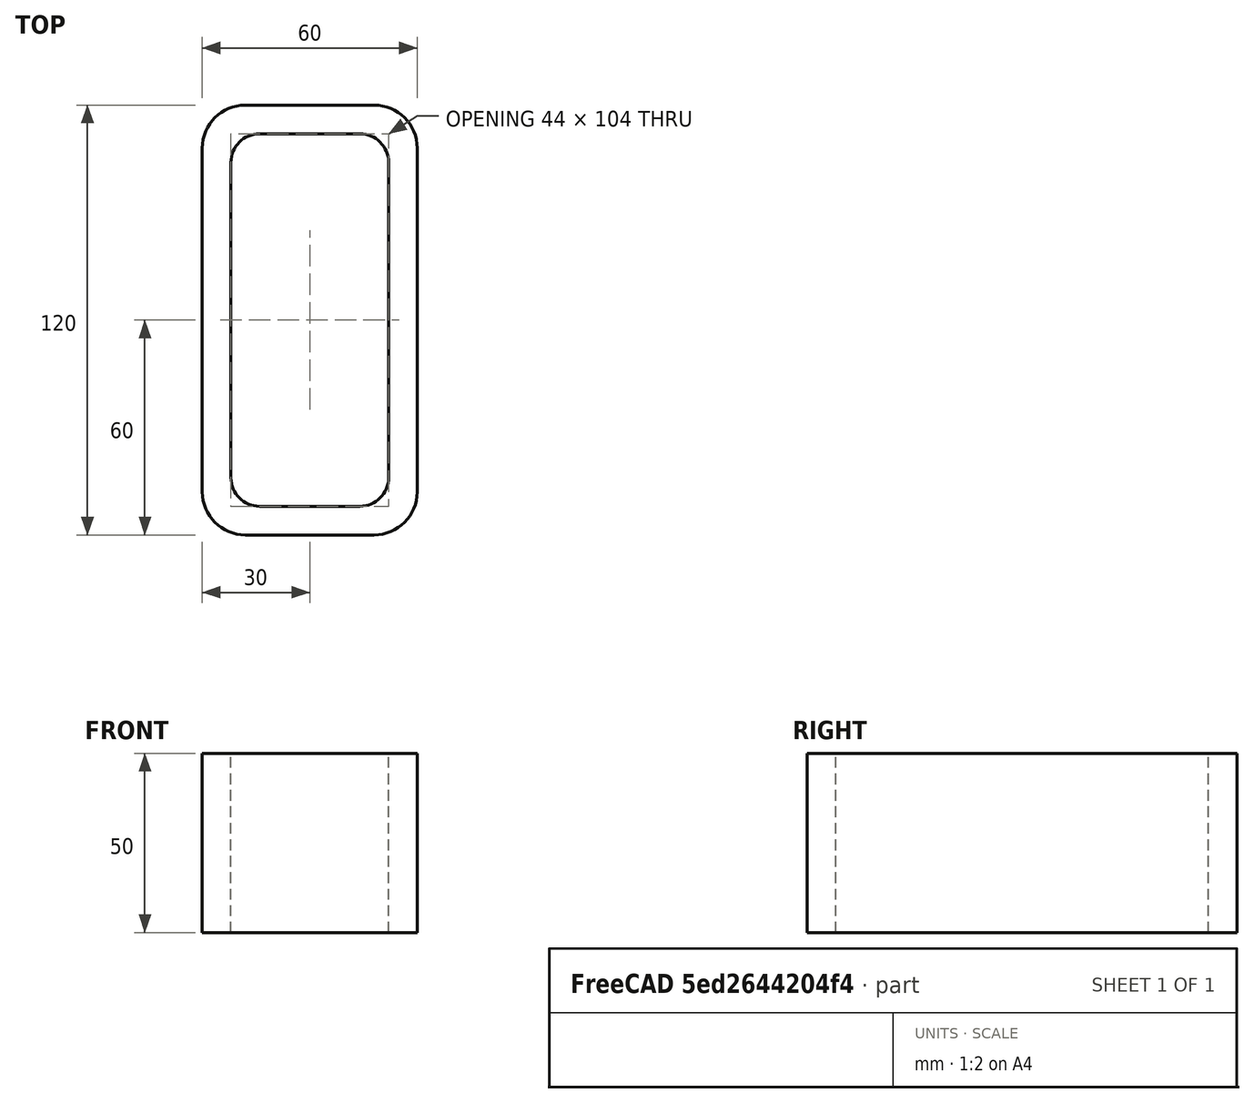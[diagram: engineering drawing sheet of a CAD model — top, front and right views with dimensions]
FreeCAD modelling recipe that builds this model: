
FCSTD DOCUMENT  (FreeCAD 0.15R4671 (Git))
Label: Rectangular hollow section 120x60x8 EN10219 S235JRH
License: All rights reserved
LicenseURL: http://en.wikipedia.org/wiki/All_rights_reserved
objects: Sketcher::SketchObject×1, Part::Extrusion×1
note: 2 computed .brp shape members not serialized (recipe doc carries the construction recipe); baked Part::Feature solids carry a one-line shape summary decoded from their .brp

FEATURE [Sketcher::SketchObject] Sketch
  sketch-geometry (16):
    g0: LineSegment StartX=-14 StartY=52 StartZ=0 EndX=14 EndY=52 EndZ=0
    g1: LineSegment StartX=22 StartY=44 StartZ=0 EndX=22 EndY=-44 EndZ=0
    g2: LineSegment StartX=14 StartY=-52 StartZ=0 EndX=-14 EndY=-52 EndZ=0
    g3: LineSegment StartX=-22 StartY=-44 StartZ=0 EndX=-22 EndY=44 EndZ=0
    g4: LineSegment StartX=-18 StartY=60 StartZ=0 EndX=18 EndY=60 EndZ=0
    g5: LineSegment StartX=30 StartY=48 StartZ=0 EndX=30 EndY=-48 EndZ=0
    g6: LineSegment StartX=18 StartY=-60 StartZ=0 EndX=-18 EndY=-60 EndZ=0
    g7: LineSegment StartX=-30 StartY=-48 StartZ=0 EndX=-30 EndY=48 EndZ=0
    g8: ArcOfCircle CenterX=-14 CenterY=44 CenterZ=0 NormalX=0 NormalY=0 NormalZ=1 Radius=8 StartAngle=1.5708 EndAngle=3.14159
    g9: ArcOfCircle CenterX=14 CenterY=44 CenterZ=0 NormalX=0 NormalY=0 NormalZ=1 Radius=8 StartAngle=0 EndAngle=1.5708
    g10: ArcOfCircle CenterX=14 CenterY=-44 CenterZ=0 NormalX=0 NormalY=0 NormalZ=1 Radius=8 StartAngle=4.71239 EndAngle=6.28319
    g11: ArcOfCircle CenterX=-14 CenterY=-44 CenterZ=0 NormalX=0 NormalY=0 NormalZ=1 Radius=8 StartAngle=3.14159 EndAngle=4.71239
    g12: ArcOfCircle CenterX=18 CenterY=48 CenterZ=0 NormalX=0 NormalY=0 NormalZ=1 Radius=12 StartAngle=0 EndAngle=1.5708
    g13: ArcOfCircle CenterX=18 CenterY=-48 CenterZ=0 NormalX=0 NormalY=0 NormalZ=1 Radius=12 StartAngle=4.71239 EndAngle=6.28319
    g14: ArcOfCircle CenterX=-18 CenterY=-48 CenterZ=0 NormalX=0 NormalY=0 NormalZ=1 Radius=12 StartAngle=3.14159 EndAngle=4.71239
    g15: ArcOfCircle CenterX=-18 CenterY=48 CenterZ=0 NormalX=0 NormalY=0 NormalZ=1 Radius=12 StartAngle=1.5708 EndAngle=3.14159
  constraints (36):
    c: Horizontal(g2)
    c: Vertical(g3)
    c: Horizontal(g6)
    c: Vertical(g7)
    c: Tangent(g3,g8) = 1.5708
    c: Tangent(g0,g8) = 1.5708
    c: Tangent(g0,g9) = 1.5708
    c: Tangent(g1,g9) = 1.5708
    c: Tangent(g1,g10) = 1.5708
    c: Tangent(g2,g10) = 1.5708
    c: Tangent(g2,g11) = 1.5708
    c: Tangent(g3,g11) = 1.5708
    c: Tangent(g4,g12) = 1.5708
    c: Tangent(g5,g12) = 1.5708
    c: Tangent(g5,g13) = 1.5708
    c: Tangent(g6,g13) = 1.5708
    c: Tangent(g6,g14) = 1.5708
    c: Tangent(g7,g14) = 1.5708
    c: Tangent(g7,g15) = 1.5708
    c: Tangent(g4,g15) = 1.5708
    c: Equal(g9,g8)
    c: Equal(g9,g11)
    c: Equal(g9,g10)
    c: Equal(g12,g15)
    c: Equal(g12,g14)
    c: Equal(g12,g13)
    c: Symmetric(g4,g6,g-1)
    c: Symmetric(g7,g5,g-2)
    c: DistanceY(g4,g6) = -120
    c: DistanceX(g7,g5) = 60
    c: Symmetric(g3,g1,g-2)
    c: Symmetric(g0,g2,g-1)
    c: DistanceY(g0,g4) = 8
    c: DistanceX(g5,g1) = -8
    c: Radius(g9) = 8
    c: Radius(g12) = 12
FEATURE [Part::Extrusion] Extrude  label="Rectangular hollow section 120x60x8 EN10219 S235JRH"
  Base = -> Sketch
  Dir = (0,0,50)
  Solid = true
